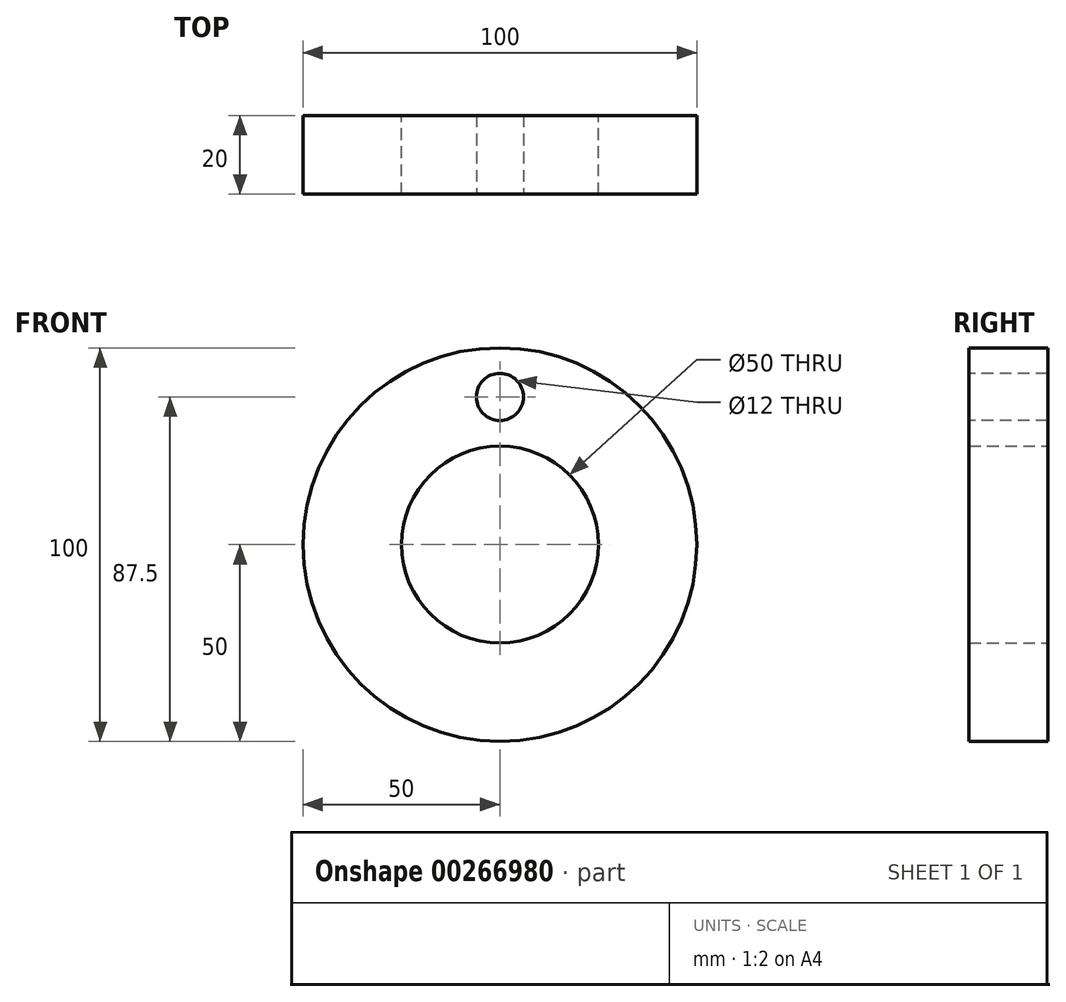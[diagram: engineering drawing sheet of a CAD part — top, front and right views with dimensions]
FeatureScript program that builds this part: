
annotation { "Feature Type Name" : "Feature", "Feature Type Description" : "" }
export const myFeature = defineFeature(function(context is Context, id is Id, definition is map)
    precondition{}
    {
        {
            var Q0;
            Q0=qCreatedBy(makeId("Front.planeOp"),FACE);
            var sketch = newSketch(context, id + "F0", { "sketchPlane" : qUnion([Q0])});
            skCircle(sketch, "E0", {"center": v(0, 0) * mm, "radius": 25 * mm});
            skCircle(sketch, "E1", {"center": v(0, 0) * mm, "radius": 50 * mm});
            skSolve(sketch);
        }
        {
            var Q0;
            Q0 = qSketchRegion(id + "F0", true);
            extrude(context, id + "F1", {"entities" : qUnion([Q0]), "depth" : 20 * mm});
        }
        {
            var Q0;
            Q0=makeQuery(id+"F1.opExtrude","CAP_FACE",FACE,{"disambiguationData":[OSD([sQuery(id+"F0.wireOp",EDGE,"E0"),sQuery(id+"F0.wireOp",EDGE,"E1")])],"isStart":false});
            var sketch = newSketch(context, id + "F2", { "sketchPlane" : qUnion([Q0])});
            skCircle(sketch, "E2", {"center": v(0, 37.5) * mm, "radius": 6 * mm});
            skCircle(sketch, "E3", {"center": v(0, 0) * mm, "radius": 37.5 * mm, "construction": true});
            skSolve(sketch);
        }
        {
            var Q0;
            Q0 = qSketchRegion(id + "F2", true);
            extrude(context, id + "F3", {"entities" : qUnion([Q0]), "operationType" : NewBodyOperationType.REMOVE, "oppositeDirection" : true, "depth" : 25 * mm});
        }
    });
